# Revit family: NLRS_57_DUF_UN_9mm_dampdichte_ronde_bocht_LT_velu
name_source: partatom
category: Duct Fittings
units: mm (PartAtom-declared; Revit-internal decimal feet)

## family parameters
Always vertical = Yes
Cut with Voids When Loaded = No
Part Type = Elbow
Round Connector Dimension = Use Diameter
Shared = No
Work Plane-Based = No

## types (1)
- SB_EDI
    Assembly Code = 57.0
    Default Elevation = 0 mm  [stored 0 ft]
    Description = Velu Dampdicht, ronde bocht, glad of segment, R=D
    IfcDescription = Velu Dampdicht, ronde bocht, glad of segment, R=D
    IfcExportAs = IfcDuctFittingType
    IfcExportType = BEND
    Manufacturer = Velu Klimaattechnische groothandel
    Model = Velu dampdicht -  ronde bocht
    NLRS_C_content_datum_gewijzigd = 16-01-2023
    NLRS_C_content_provider = Velu Klimaattechnische groothandel
    NLRS_C_content_versie = 3.20.01
    Type Comments = 9mm dampdichte isolatie toevoegen via Revit Insulation - Isolatie is voorgemonteerd op kanaalstuk.
    Type Image = <None>
    URL = https://velu.nl

note: [stored X ft] marks values corroborated as IEEE doubles in the binary element streams (Revit-internal decimal feet)

## geometry (parser evidence)
native form markers: Sweep x6
no freeform markers — native parametric forms only
